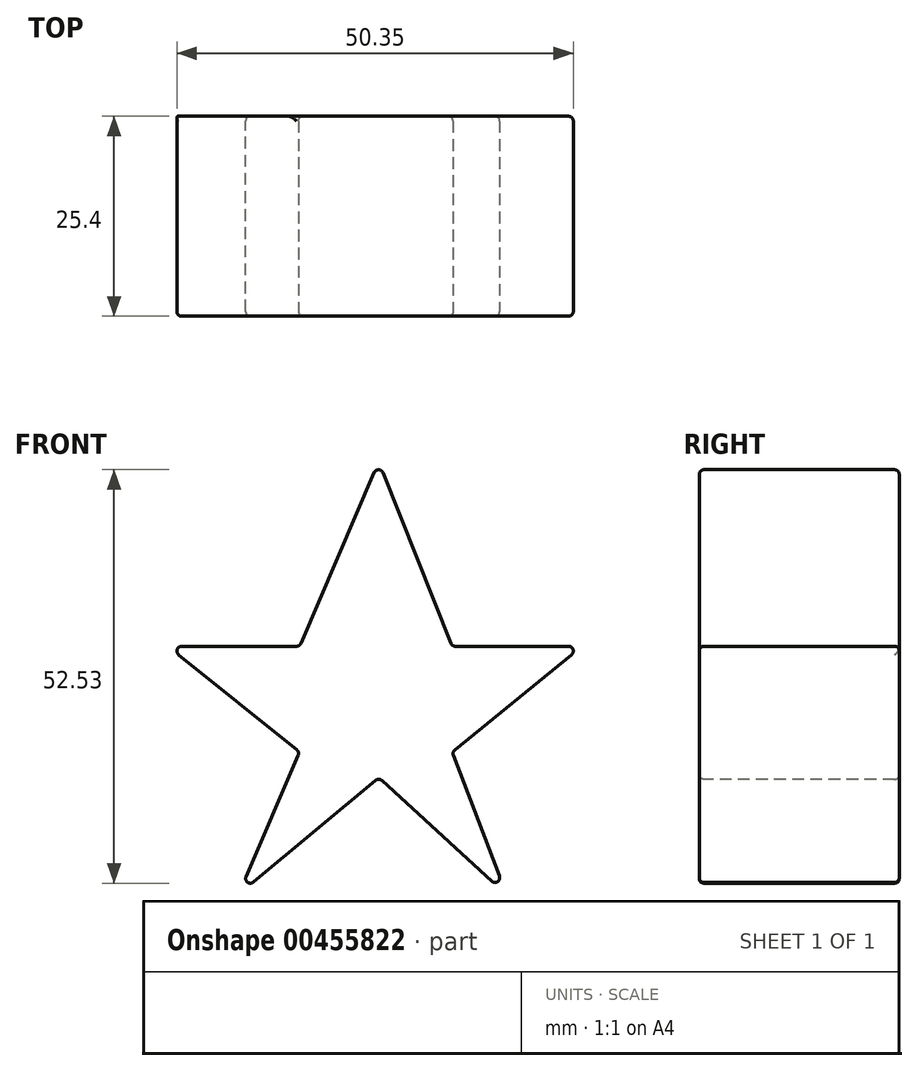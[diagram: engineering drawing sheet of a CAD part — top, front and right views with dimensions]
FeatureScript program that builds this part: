
annotation { "Feature Type Name" : "Feature", "Feature Type Description" : "" }
export const myFeature = defineFeature(function(context is Context, id is Id, definition is map)
    precondition{}
    {
        {
            var Q0;
            Q0=qCreatedBy(makeId("Front.planeOp"),FACE);
            var sketch = newSketch(context, id + "F0", { "sketchPlane" : qUnion([Q0])});
            skLineSegment(sketch, "E0", {"start": v(0, 31.7) * mm, "end": v(-10.06, 8.3) * mm});
            skLineSegment(sketch, "E1", {"start": v(0, 31.7) * mm, "end": v(9.32, 8.3) * mm});
            skLineSegment(sketch, "E2", {"start": v(9.32, 8.3) * mm, "end": v(25.8, 8.3) * mm});
            skLineSegment(sketch, "E3", {"start": v(9.32, 8.3) * mm, "end": v(25.8, 8.3) * mm, "construction": true});
            skLineSegment(sketch, "E4", {"start": v(-10.06, 8.3) * mm, "end": v(-26.73, 8.3) * mm});
            skLineSegment(sketch, "E5", {"start": v(-26.73, 8.3) * mm, "end": v(-10.06, -5.16) * mm});
            skLineSegment(sketch, "E6", {"start": v(25.8, 8.3) * mm, "end": v(9.32, -5.16) * mm});
            skLineSegment(sketch, "E7", {"start": v(-10.06, -5.16) * mm, "end": v(-17.84, -23.26) * mm});
            skLineSegment(sketch, "E8", {"start": v(9.32, -5.16) * mm, "end": v(16.23, -23.26) * mm});
            skLineSegment(sketch, "E9", {"start": v(-17.84, -23.26) * mm, "end": v(0, -8.4) * mm});
            skLineSegment(sketch, "E10", {"start": v(0, -8.4) * mm, "end": v(16.23, -23.26) * mm});
            skSolve(sketch);
        }
        {
            var Q0;
            Q0=makeQuery(id+"F0.imprint","IMPRINT",FACE,{"disambiguationData":[TD([[makeQuery(id+"F0.imprint","IMPRINT",EDGE,{"derivedFrom":sQuery(id+"F0.wireOp",EDGE,"E0")}),1.0]])]});
            extrude(context, id + "F1", {"entities" : qUnion([Q0]), "depth" : 25.4 * mm});
        }
        {
            var Q0;
            Q0=makeQuery(id+"F1.opExtrude","CAP_FACE",FACE,{"disambiguationData":[OSD([sQuery(id+"F0.wireOp",EDGE,"E0"),sQuery(id+"F0.wireOp",EDGE,"E1"),sQuery(id+"F0.wireOp",EDGE,"E2"),sQuery(id+"F0.wireOp",EDGE,"E4"),sQuery(id+"F0.wireOp",EDGE,"E5"),sQuery(id+"F0.wireOp",EDGE,"E6"),sQuery(id+"F0.wireOp",EDGE,"E7"),sQuery(id+"F0.wireOp",EDGE,"E8"),sQuery(id+"F0.wireOp",EDGE,"E9"),sQuery(id+"F0.wireOp",EDGE,"E10")])],"isStart":false});
            var Q1;
            Q1=makeQuery(id+"F1.opExtrude","SWEPT_FACE",FACE,{"disambiguationData":[OSD([sQuery(id+"F0.wireOp",EDGE,"E2")])]});
            var Q2;
            Q2=makeQuery(id+"F1.opExtrude","SWEPT_FACE",FACE,{"disambiguationData":[OSD([sQuery(id+"F0.wireOp",EDGE,"E1")])]});
            var Q3;
            Q3=makeQuery(id+"F1.opExtrude","SWEPT_FACE",FACE,{"disambiguationData":[OSD([sQuery(id+"F0.wireOp",EDGE,"E0")])]});
            var Q4;
            Q4=makeQuery(id+"F1.opExtrude","SWEPT_FACE",FACE,{"disambiguationData":[OSD([sQuery(id+"F0.wireOp",EDGE,"E7")])]});
            var Q5;
            Q5=makeQuery(id+"F1.opExtrude","SWEPT_FACE",FACE,{"disambiguationData":[OSD([sQuery(id+"F0.wireOp",EDGE,"E5")])]});
            var Q6;
            Q6=makeQuery(id+"F1.opExtrude","SWEPT_FACE",FACE,{"disambiguationData":[OSD([sQuery(id+"F0.wireOp",EDGE,"E10")])]});
            var Q7;
            Q7=makeQuery(id+"F1.opExtrude","SWEPT_FACE",FACE,{"disambiguationData":[OSD([sQuery(id+"F0.wireOp",EDGE,"E9")])]});
            var Q8;
            Q8=makeQuery(id+"F1.opExtrude","SWEPT_FACE",FACE,{"disambiguationData":[OSD([sQuery(id+"F0.wireOp",EDGE,"E6")])]});
            var Q9;
            Q9=makeQuery(id+"F1.opExtrude","SWEPT_FACE",FACE,{"disambiguationData":[OSD([sQuery(id+"F0.wireOp",EDGE,"E8")])]});
            var Q10;
            Q10=makeQuery(id+"F1.opExtrude","CAP_EDGE",EDGE,{"disambiguationData":[OSD([sQuery(id+"F0.wireOp",EDGE,"E9")])],"isStart":true});
            fillet(context, id + "F2", {"entities" : qUnion([Q0, Q1, Q2, Q3, Q4, Q5, Q6, Q7, Q8, Q9, Q10]), "radius" : 0.6 * mm, "tangentPropagation" : true, "allowEdgeOverflow" : false});
        }
    });
